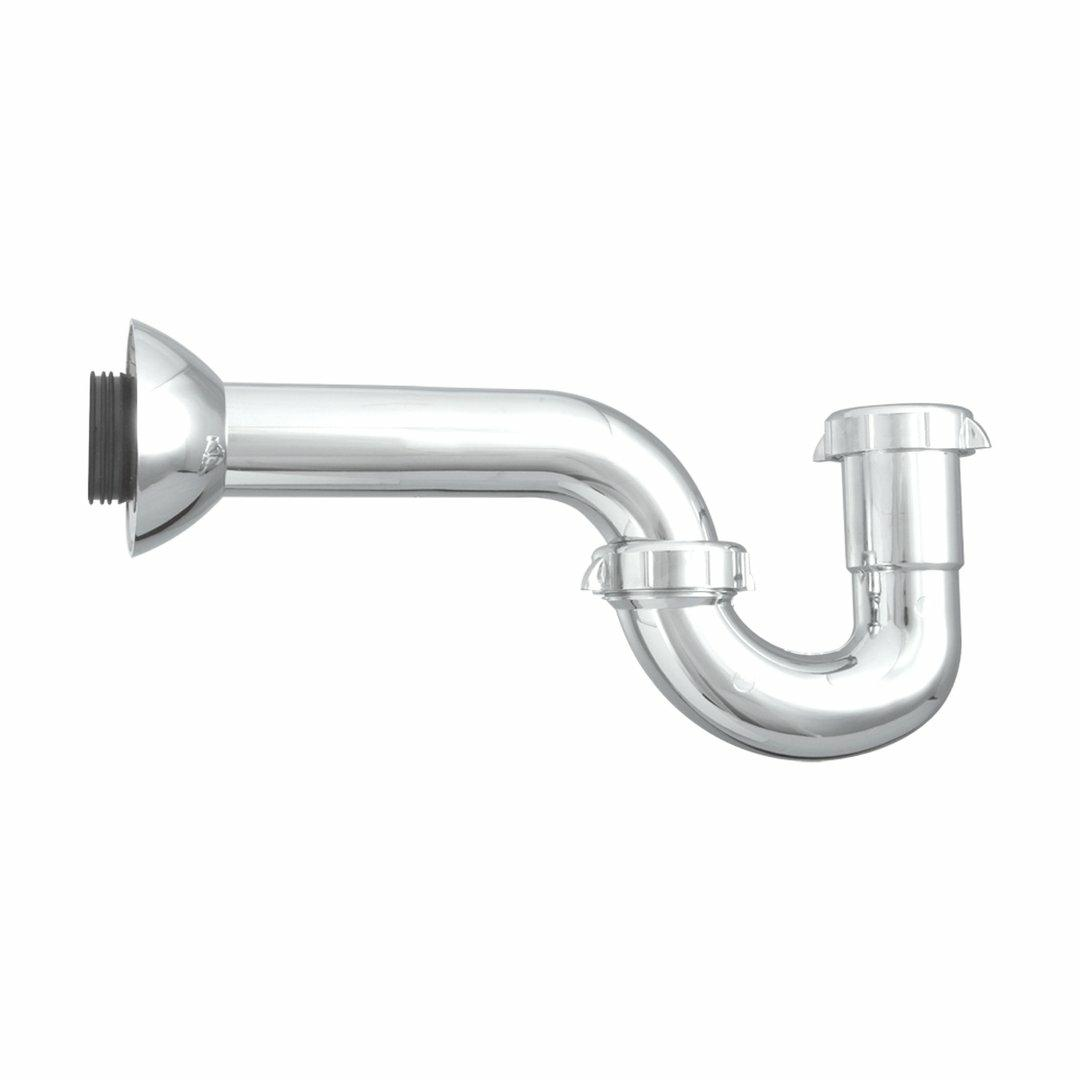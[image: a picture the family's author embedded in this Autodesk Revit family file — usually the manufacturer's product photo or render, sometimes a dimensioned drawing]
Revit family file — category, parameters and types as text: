
# Revit family: BIM_M1-3002-11
name_source: partatom
category: Aparatos sanitarios
units: mm (PartAtom-declared; Revit-internal decimal feet)

## family parameters
Activar corte en vistas = No
Anfitrión = Cara
Compartido = No
Corte con vacíos al cargar = No
Cota de conector redondo = Usar diámetro
Mantener orientación de anotación = No
Número OmniClass = 23.31.11.00
Punto de cálculo de habitación = No
Tipo de pieza = Normal

## types (1)
- M1-3002-11
    Acabado = Cepillado Brillante
    Alto = 185 mm  [stored 0.606955 ft]
    Ancho = 840 mm
    Conexión AC = Sí
    Conexión AF = Sí
    Conexión de residuos = No
    Conexión de ventilación = No
    Date Modified = 08-08-2025
    Descripción = Lavaplatos doble en acero
    Elevación por defecto = 0 mm  [stored 0 ft]
    Fabricante = Gricol
    Garantia Especifica = 5 años
    Imagen de tipo = FOTO-LAVAPLATOS EN ACERO DOBLE POCETA 84 x 56 cm.jpg
    Largo = 560 mm  [stored 1.83727 ft]
    Link Ficha Tecnica = https://infotecnica.gricol.com
    Material = Acero inoxidable
    Materiales del producto = Acero Inoxidable
    Modelo = M1-3002-11
    Nota clave = Perforación para instalar grifería 8”
    Peso = 3.32 kg
    Product Name = Lavaplatos De Empotrar Doble Poceta 84 X 56 Cm Con Complementos Para Mezclador
    Resistencia a Corrosión = Si
    Sitio web = https://www.gricol.com
    Tipo de Uso = Residencial
    URL = https://www.gricol.com

note: [stored X ft] marks values corroborated as IEEE doubles in the binary element streams (Revit-internal decimal feet)

## geometry (parser evidence)
native form markers: Blend x2, Sweep x12
no freeform markers — native parametric forms only
